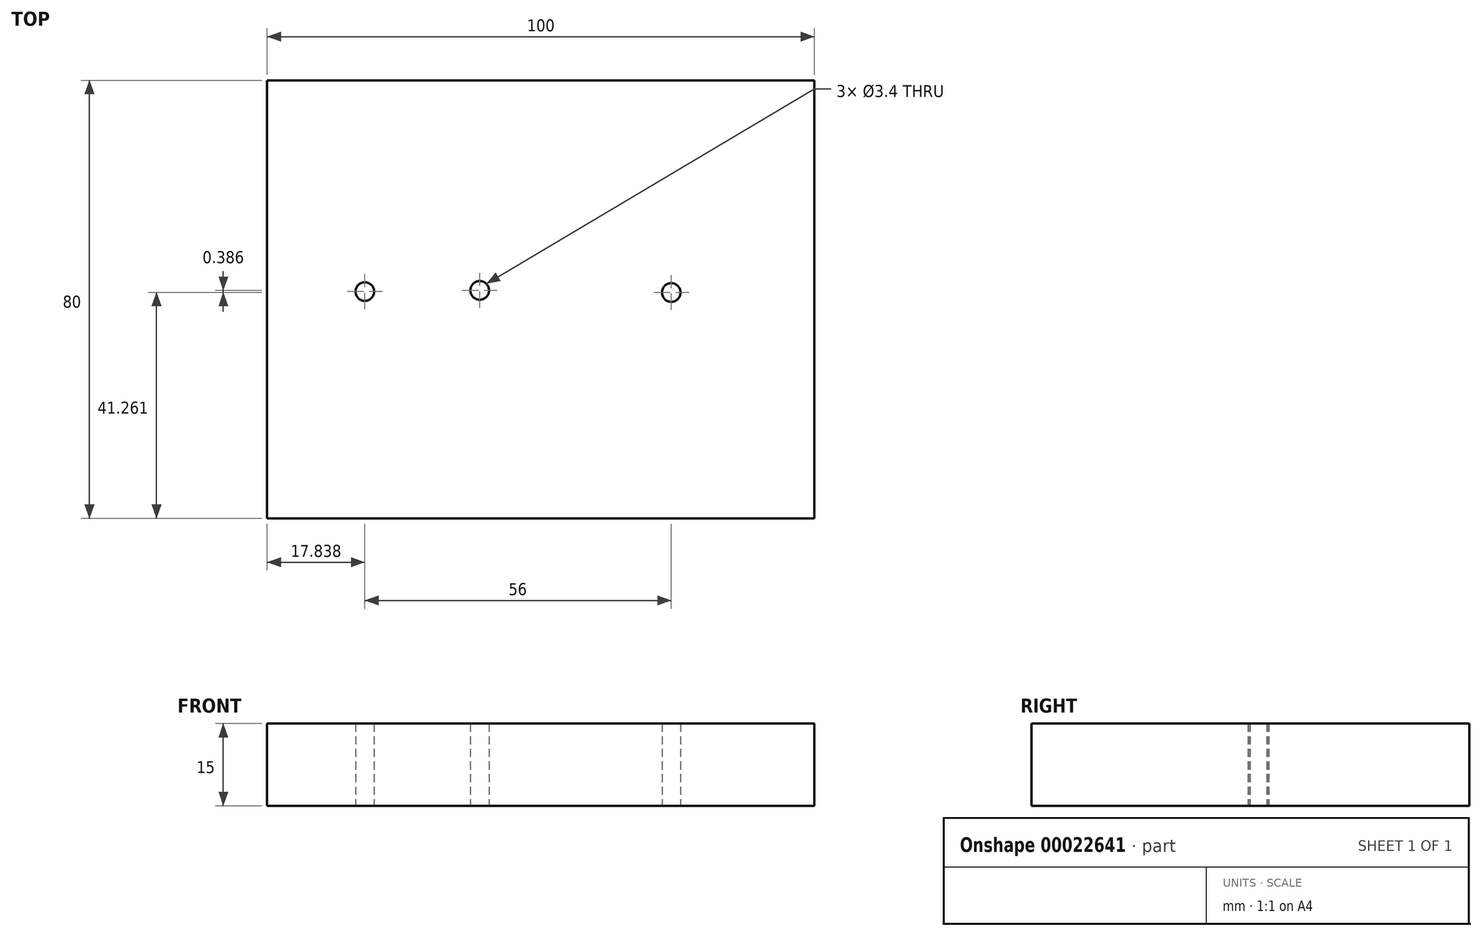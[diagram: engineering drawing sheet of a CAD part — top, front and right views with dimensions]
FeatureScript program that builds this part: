
annotation { "Feature Type Name" : "Feature", "Feature Type Description" : "" }
export const myFeature = defineFeature(function(context is Context, id is Id, definition is map)
    precondition{}
    {
        {
            var Q0;
            Q0=qCreatedBy(makeId("Top.planeOp"),FACE);
            var sketch = newSketch(context, id + "F0", { "sketchPlane" : qUnion([Q0])});
            skLineSegment(sketch, "E0.bottom", {"start": v(-73.54, 38.57) * mm, "end": v(26.46, 38.57) * mm});
            skLineSegment(sketch, "E0.top", {"start": v(-73.54, -41.43) * mm, "end": v(26.46, -41.43) * mm});
            skLineSegment(sketch, "E0.left", {"start": v(-73.54, 38.57) * mm, "end": v(-73.54, -41.43) * mm});
            skLineSegment(sketch, "E0.right", {"start": v(26.46, 38.57) * mm, "end": v(26.46, -41.43) * mm});
            skCircle(sketch, "E1", {"center": v(-55.7, 0) * mm, "radius": 1.7 * mm});
            skCircle(sketch, "E2", {"center": v(-34.7, 0.22) * mm, "radius": 1.7 * mm});
            skCircle(sketch, "E3", {"center": v(0.3, -0.17) * mm, "radius": 1.7 * mm});
            skSolve(sketch);
        }
        {
            var Q0;
            Q0=makeQuery(id+"F0.imprint","IMPRINT",FACE,{"disambiguationData":[TD([[makeQuery(id+"F0.imprint","IMPRINT",EDGE,{"derivedFrom":sQuery(id+"F0.wireOp",EDGE,"E0.bottom")}),-1.0]])]});
            extrude(context, id + "F1", {"entities" : qUnion([Q0]), "depth" : 15 * mm});
        }
    });
